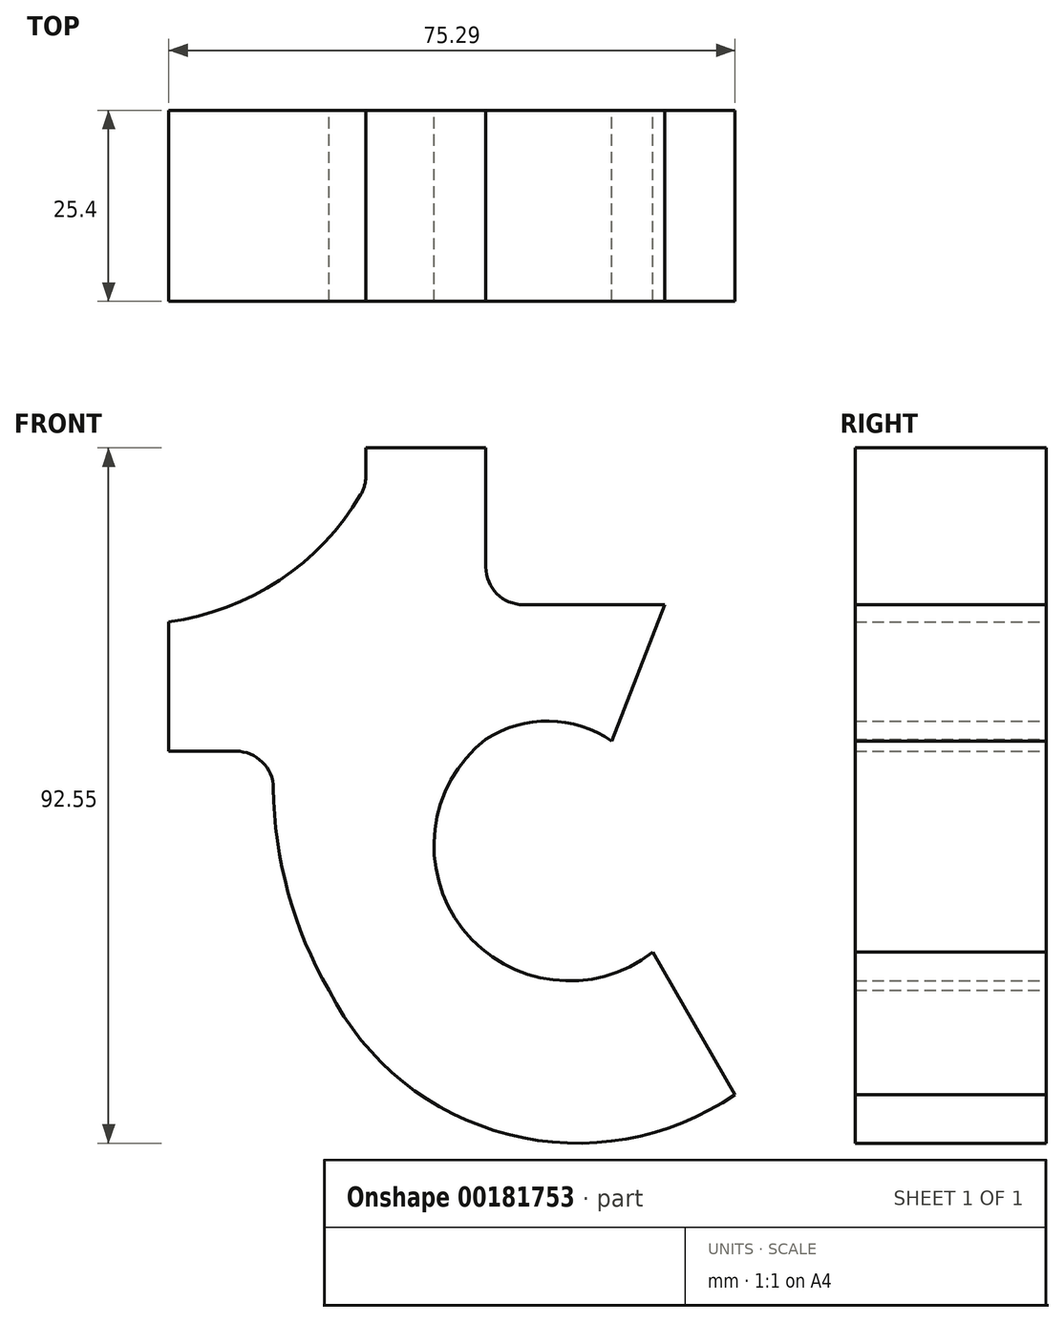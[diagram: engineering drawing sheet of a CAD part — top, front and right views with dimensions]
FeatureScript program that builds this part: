
annotation { "Feature Type Name" : "Feature", "Feature Type Description" : "" }
export const myFeature = defineFeature(function(context is Context, id is Id, definition is map)
    precondition{}
    {
        {
            var Q0;
            Q0=qCreatedBy(makeId("Front.planeOp"),FACE);
            var sketch = newSketch(context, id + "F0", { "sketchPlane" : qUnion([Q0])});
            skText(sketch, "E0", { "text": "t", "fontName": "RobotoSlab-Bold.ttf"});
            const initialGuessF0  = {"E0": [-0.0626, -0.05378, 1, 0, 0.109]};
            skSetInitialGuess(sketch, initialGuessF0);
            skSolve(sketch);
        }
        {
            var Q0;
            Q0=makeQuery(id+"F0.imprint","IMPRINT",FACE,{"disambiguationData":[TD([[makeQuery(id+"F0.imprint","IMPRINT",EDGE,{"derivedFrom":sQuery(id+"F0.wireOp",EDGE,"E0.sketch_text.stroke-0")}),-1.0]])]});
            var sketch = newSketch(context, id + "F1", { "sketchPlane" : qUnion([Q0])});
            skLineSegment(sketch, "E1", {"start": v(-44.06, 46.21) * mm, "end": v(-27.3, 46.21) * mm});
            skLineSegment(sketch, "E2", {"start": v(-27.3, 46.21) * mm, "end": v(-27.3, 29.9) * mm});
            skLineSegment(sketch, "E3", {"start": v(-27.3, 29.9) * mm, "end": v(-3.48, 29.9) * mm});
            skLineSegment(sketch, "E4", {"start": v(-5.08, -16.34) * mm, "end": v(5.84, -35.3) * mm});
            skLineSegment(sketch, "E5", {"start": v(-55.4, 10.4) * mm, "end": v(-69.45, 10.4) * mm});
            skLineSegment(sketch, "E6", {"start": v(-69.45, 10.4) * mm, "end": v(-69.45, 27.63) * mm});
            skArc(sketch, "E7", {"start": v(-27.3, 12) * mm, "mid": v(-30.36, -13.27) * mm, "end": v(-5.08, -16.34) * mm});
            skArc(sketch, "E8", {"start": v(-48.16, -21.43) * mm, "mid": v(-24.3, -40.6) * mm, "end": v(5.84, -35.3) * mm});
            skLineSegment(sketch, "E9", {"start": v(-3.48, 29.9) * mm, "end": v(-10.52, 11.76) * mm});
            skArc(sketch, "E10", {"start": v(-55.4, 10.4) * mm, "mid": v(-54.17, -6.06) * mm, "end": v(-48.16, -21.43) * mm});
            skArc(sketch, "E11", {"start": v(-10.52, 11.76) * mm, "mid": v(-18.87, 14.42) * mm, "end": v(-27.3, 12) * mm});
            skArc(sketch, "E12", {"start": v(-69.45, 27.63) * mm, "mid": v(-53.96, 33.68) * mm, "end": v(-43.02, 46.21) * mm});
            skSolve(sketch);
        }
        {
            var Q0;
            Q0=makeQuery(id+"F1.imprint","IMPRINT",FACE,{"disambiguationData":[TD([[makeQuery(id+"F1.imprint","IMPRINT",EDGE,{"derivedFrom":sQuery(id+"F1.wireOp",EDGE,"E5")}),-1.0]])]});
            var Q1;
            {var subQ24=makeQuery(id+"F0.imprint","IMPRINT",EDGE,{"derivedFrom":sQuery(id+"F0.wireOp",EDGE,"E0.sketch_text.stroke-1")});Q1=makeQuery(id+"F1.imprint","IMPRINT",FACE,{"disambiguationData":[TD([[makeQuery(id+"F1.imprint","IMPRINT",EDGE,{"derivedFrom":subQ24}),-1.0]])]});}
            var Q2;
            {var subQ1=sQuery(id+"F1.wireOp",EDGE,"E9");Q2=makeQuery(id+"F1.imprint","IMPRINT",FACE,{"disambiguationData":[TD([[makeQuery(id+"F1.imprint","IMPRINT",EDGE,{"derivedFrom":subQ1}),-1.0]])]});}
            var Q3;
            {var subQ1=sQuery(id+"F1.wireOp",EDGE,"E4");Q3=makeQuery(id+"F1.imprint","IMPRINT",FACE,{"disambiguationData":[TD([[makeQuery(id+"F1.imprint","IMPRINT",EDGE,{"derivedFrom":subQ1}),-1.0]])]});}
            extrude(context, id + "F2", {"entities" : qUnion([Q0, Q1, Q2, Q3]), "depth" : 25.4 * mm});
        }
        {
            var Q0;
            Q0=makeQuery(id+"F2.opExtrude","SWEPT_FACE",FACE,{"disambiguationData":[OSD([sQuery(id+"F0.wireOp",EDGE,"E0.sketch_text.stroke-19")])]});
            extrude(context, id + "F3", {"entities" : qUnion([Q0]), "operationType" : NewBodyOperationType.ADD, "depth" : 5 * mm});
        }
        {
            var Q0;
            Q0=makeQuery(id+"F2.opExtrude","SWEPT_EDGE",EDGE,{"disambiguationData":[OSD([sQuery(id+"F1.wireOp",EDGE,"E2"),sQuery(id+"F1.wireOp",EDGE,"E3")])]});
            var Q1;
            {var subQ0=sQuery(id+"F1.wireOp",EDGE,"E12");var subQ1=sQuery(id+"F0.wireOp",EDGE,"E0.sketch_text.stroke-19");Q1=makeQuery(id+"F3.boolean.opBoolean","MERGE",EDGE,{"derivedFrom":[makeQuery(id+"F2.opExtrude","SWEPT_EDGE",EDGE,{"disambiguationData":[OSD([subQ1,subQ0])]}),makeQuery(id+"F3.opExtrude","CAP_EDGE",EDGE,{"disambiguationData":[OSD([subQ1,subQ0])],"isStart":true})]});}
            var Q2;
            Q2=makeQuery(id+"F2.opExtrude","SWEPT_EDGE",EDGE,{"disambiguationData":[OSD([sQuery(id+"F1.wireOp",EDGE,"E5"),sQuery(id+"F1.wireOp",EDGE,"E10")])]});
            fillet(context, id + "F4", {"entities" : qUnion([Q0, Q1, Q2]), "radius" : 5 * mm, "tangentPropagation" : true, "allowEdgeOverflow" : false});
        }
        {
            var Q0;
            Q0=makeQuery(id+"F2.opExtrude","SWEPT_BODY",BODY,{"disambiguationData":[OSD([sQuery(id+"F0.wireOp",EDGE,"E0.sketch_text.stroke-19"),sQuery(id+"F1.wireOp",EDGE,"E2"),sQuery(id+"F1.wireOp",EDGE,"E3"),sQuery(id+"F1.wireOp",EDGE,"E4"),sQuery(id+"F1.wireOp",EDGE,"E5"),sQuery(id+"F1.wireOp",EDGE,"E6"),sQuery(id+"F1.wireOp",EDGE,"E7"),sQuery(id+"F1.wireOp",EDGE,"E8"),sQuery(id+"F1.wireOp",EDGE,"E9"),sQuery(id+"F1.wireOp",EDGE,"E10"),sQuery(id+"F1.wireOp",EDGE,"E11"),sQuery(id+"F1.wireOp",EDGE,"E12")])]});
            transform(context, id + "F5", {"entities" : qUnion([Q0]), "transformType" : TransformType.TRANSLATION_3D, "dx" : 0 * mm, "dy" : 0 * mm, "dz" : 0 * mm, "makeCopy" : true});
        }
    });
